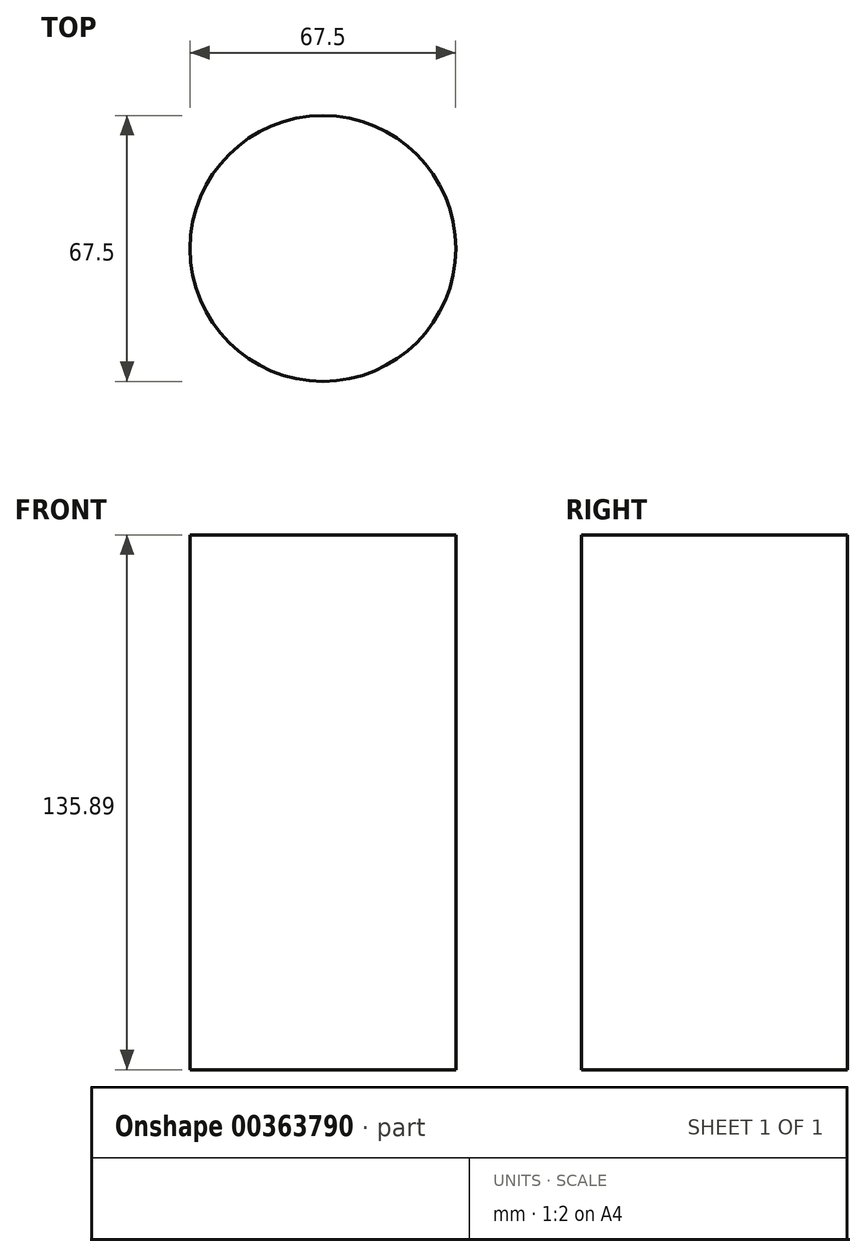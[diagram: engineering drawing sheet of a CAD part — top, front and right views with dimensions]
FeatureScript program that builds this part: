
annotation { "Feature Type Name" : "Feature", "Feature Type Description" : "" }
export const myFeature = defineFeature(function(context is Context, id is Id, definition is map)
    precondition{}
    {
        {
            var Q0;
            Q0=qCreatedBy(makeId("Top.planeOp"),FACE);
            var sketch = newSketch(context, id + "F0", { "sketchPlane" : qUnion([Q0])});
            skCircle(sketch, "E0", {"center": v(-2.6, 0) * mm, "radius": 33.75 * mm});
            skSolve(sketch);
        }
        {
            var Q0;
            Q0=makeQuery(id+"F0.imprint","IMPRINT",FACE,{"disambiguationData":[TD([[makeQuery(id+"F0.imprint","IMPRINT",EDGE,{"derivedFrom":sQuery(id+"F0.wireOp",EDGE,"E0")}),1.0]])]});
            extrude(context, id + "F1", {"entities" : qUnion([Q0]), "depth" : 27.18 * mm});
        }
        {
            var Q0;
            Q0=makeQuery(id+"F1.opExtrude","CAP_FACE",FACE,{"disambiguationData":[OSD([sQuery(id+"F0.wireOp",EDGE,"E0")])],"isStart":false});
            extrude(context, id + "F2", {"entities" : qUnion([Q0]), "operationType" : NewBodyOperationType.ADD, "oppositeDirection" : true, "depth" : 135.89 * mm});
        }
    });
